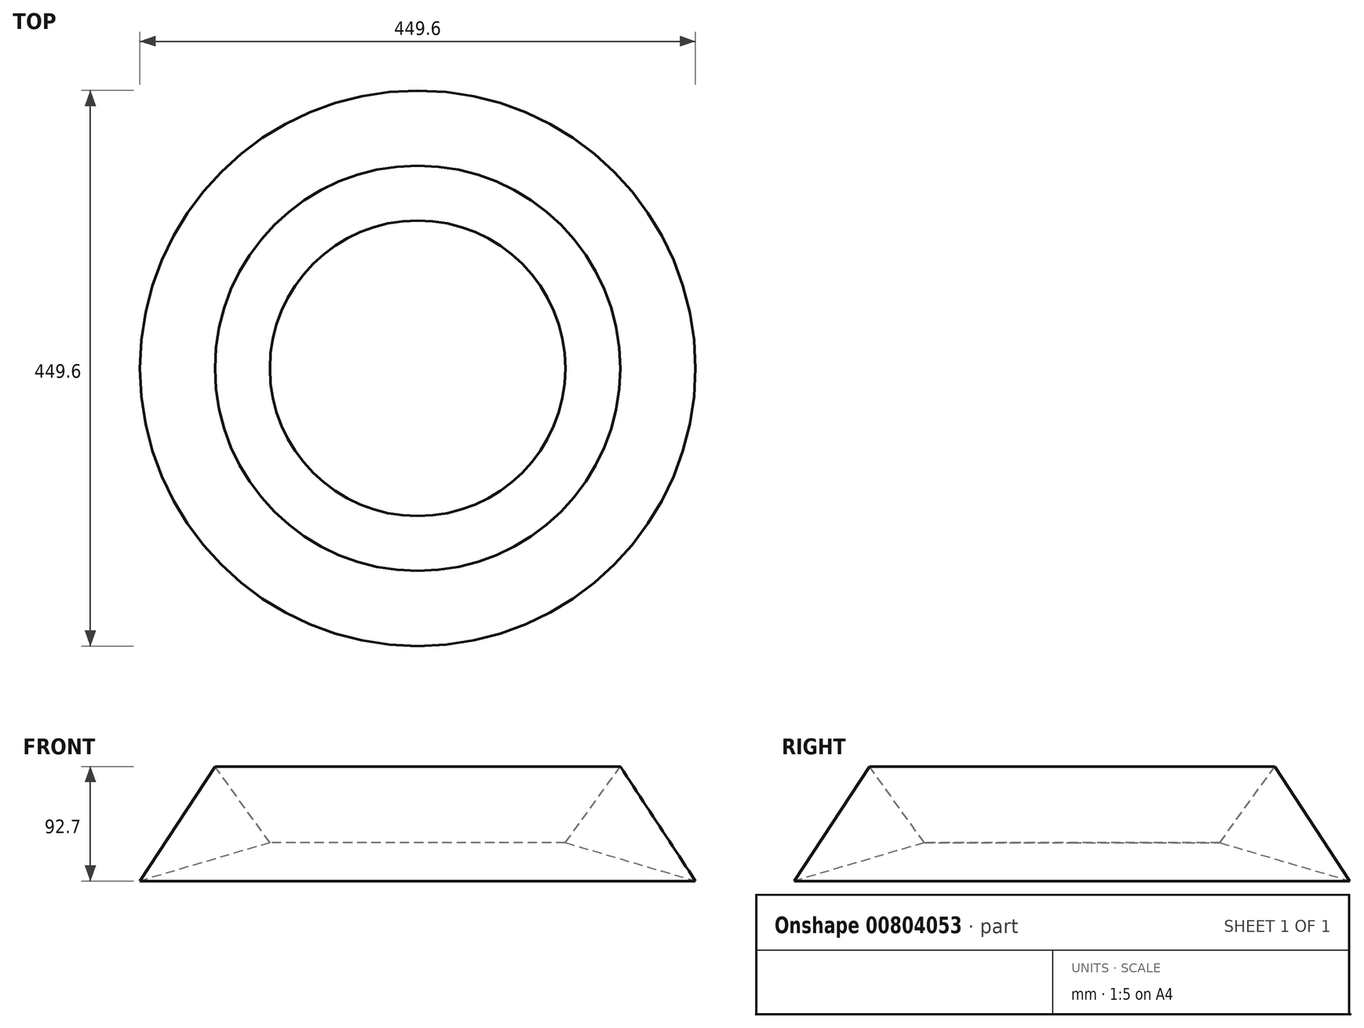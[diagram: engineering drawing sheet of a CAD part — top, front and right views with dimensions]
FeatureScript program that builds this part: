
annotation { "Feature Type Name" : "Feature", "Feature Type Description" : "" }
export const myFeature = defineFeature(function(context is Context, id is Id, definition is map)
    precondition{}
    {
        {
            var Q0;
            Q0=qCreatedBy(makeId("Front.planeOp"),FACE);
            var sketch = newSketch(context, id + "F0", { "sketchPlane" : qUnion([Q0])});
            skLineSegment(sketch, "E0", {"start": v(-28.75, 52.15) * mm, "end": v(15.68, -9.52) * mm});
            skLineSegment(sketch, "E1", {"start": v(15.68, -9.52) * mm, "end": v(-89.53, -40.55) * mm});
            skLineSegment(sketch, "E2", {"start": v(-89.53, -40.55) * mm, "end": v(-28.75, 52.15) * mm});
            skLineSegment(sketch, "E3", {"start": v(135.27, 133.48) * mm, "end": v(135.27, -80.22) * mm});
            skSolve(sketch);
        }
        {
            var Q0;
            Q0=makeQuery(id+"F0.imprint","IMPRINT",FACE,{"disambiguationData":[TD([[makeQuery(id+"F0.imprint","IMPRINT",EDGE,{"derivedFrom":sQuery(id+"F0.wireOp",EDGE,"E0")}),-1.0]])]});
            var Q1;
            Q1=sQuery(id+"F0.wireOp",EDGE,"E3");
            revolve(context, id + "F1", {"surfaceOperationType" : NewSurfaceOperationType.NEW, "entities" : qUnion([Q0]), "axis" : qUnion([Q1]), "revolveType" : RevolveType.FULL});
        }
    });
